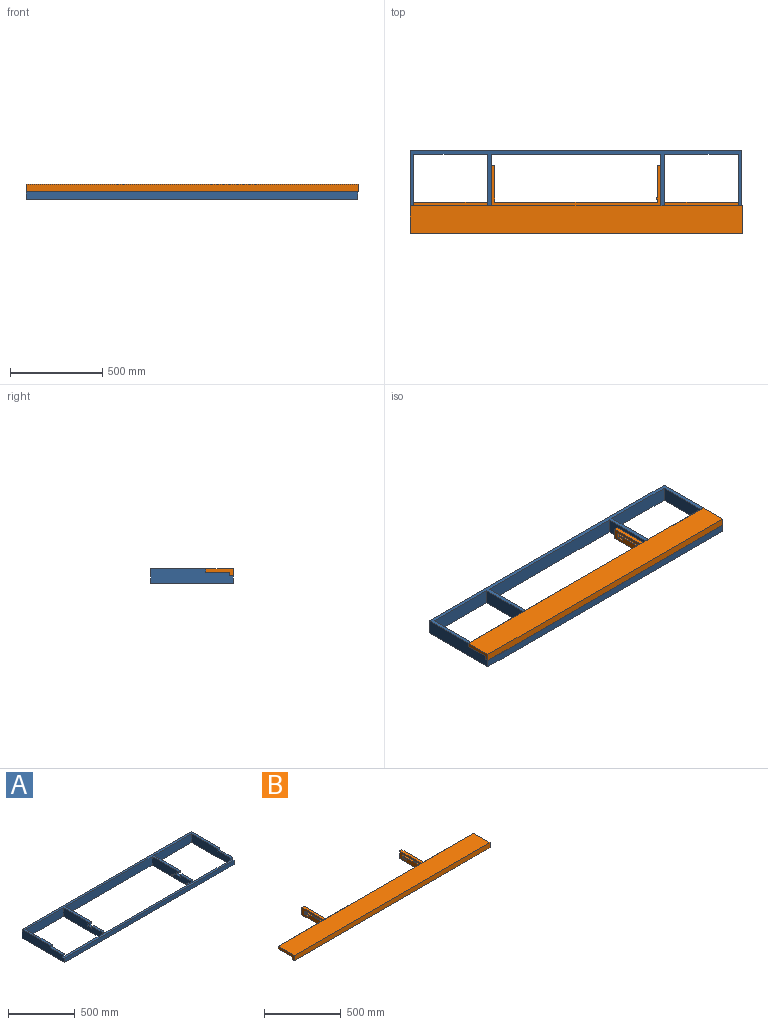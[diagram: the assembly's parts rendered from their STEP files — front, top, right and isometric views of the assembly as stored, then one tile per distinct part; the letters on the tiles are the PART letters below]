
ASSEMBLY  parts=2 mates=1
PART A: 43 faces, bbox 1800x450x80 mm
  f0: plane 410x80mm, normal (-1,0,0), area 29400mm2, adj f2,f6,f7,f12,f18,f24,f28,f39
  f1: plane 410x80mm, normal (1,0,0), area 29400mm2, adj f2,f3,f7,f14,f19,f25,f29,f35
  f2: plane 1800x300mm, normal (0,0,1), area 58400mm2, adj f0,f1,f3,f5,f8,f9,f11,f12
  f3: plane 400x80mm, normal (0,-1,0), area 32000mm2, adj f1,f2,f7,f13
  f4: plane 920x40mm, normal (0,1,0), area 36800mm2, adj f7,f16,f17,f30
  f5: plane 920x80mm, normal (0,-1,0), area 73600mm2, adj f2,f7,f16,f17
  f6: plane 400x40mm, normal (0,1,0), area 16000mm2, adj f0,f7,f15,f30
  f7: plane 1800x450mm, normal (0,0,-1), area 104800mm2, adj f0,f1,f3,f4,f5,f6,f8,f9
  f8: plane 1800x80mm, normal (0,1,0), area 144000mm2, adj f2,f7,f9,f11
  f9: plane 450x80mm, normal (1,0,0), area 32600mm2, adj f2,f7,f8,f10,f21,f22,f26,f30
  f10: plane 1800x40mm, normal (0,-1,0), area 72000mm2, adj f7,f9,f11,f30
  f11: plane 450x80mm, normal (-1,0,0), area 32600mm2, adj f2,f7,f8,f10,f20,f23,f27,f30
  f12: plane 400x80mm, normal (0,-1,0), area 32000mm2, adj f0,f2,f7,f15
  f13: plane 410x80mm, normal (-1,0,0), area 30200mm2, adj f2,f3,f7,f14,f21,f22,f26
  f14: plane 400x40mm, normal (0,1,0), area 16000mm2, adj f1,f7,f13,f30
  f15: plane 410x80mm, normal (1,0,0), area 30200mm2, adj f2,f6,f7,f12,f20,f23,f27
  f16: plane 410x80mm, normal (1,0,0), area 29400mm2, adj f2,f4,f5,f7,f18,f24,f28,f39
  f17: plane 410x80mm, normal (-1,0,0), area 29272.8mm2, adj f2,f4,f5,f7,f19,f25,f29,f31
  f18: plane 20x20mm, normal (0,-1,0), area 400mm2, adj f0,f16,f24,f30
  f19: plane 20x20mm, normal (0,-1,0), area 400mm2, adj f1,f17,f25,f30
  f20: plane 20x20mm, normal (0,-1,0), area 400mm2, adj f11,f15,f23,f30
  f21: plane 20x20mm, normal (0,-1,0), area 400mm2, adj f9,f13,f22,f30
  f22: plane 130x20mm, normal (0,0,1), area 2600mm2, adj f9,f13,f21,f26
  f23: plane 130x20mm, normal (0,0,1), area 2600mm2, adj f11,f15,f20,f27
  f24: plane 110x20mm, normal (0,0,1), area 2200mm2, adj f0,f16,f18,f40
  f25: plane 110x20mm, normal (0,0,1), area 2200mm2, adj f1,f17,f19,f38
  f26: plane 20x20mm, normal (0,-1,0), area 400mm2, adj f2,f9,f13,f22
  f27: plane 20x20mm, normal (0,-1,0), area 400mm2, adj f2,f11,f15,f23
  f28: plane 20x20mm, normal (0,-1,0), area 400mm2, adj f0,f2,f16,f39
  f29: plane 20x20mm, normal (0,-1,0), area 400mm2, adj f1,f2,f17,f35
  f30: plane 1800x20mm, normal (0,0,1), area 36000mm2, adj f4,f6,f9,f10,f11,f14,f18,f19
  f31: cylinder r=4.5mm len=25mm, axis (1,0,0), area 706.9mm2, adj f17,f32
  f32: plane 9x9mm, normal (-1,0,0), area 63.6mm2, adj f31
  f33: cylinder r=4.5mm len=25mm, axis (1,0,0), area 706.9mm2, adj f17,f34
  f34: plane 9x9mm, normal (-1,0,0), area 63.6mm2, adj f33
  f35: plane 20x20mm, normal (0,0,-1), area 400mm2, adj f1,f17,f29,f36
  f36: plane 20x20mm, normal (0,-1,0), area 400mm2, adj f1,f17,f35,f37
  f37: plane 40x20mm, normal (0,0,1), area 800mm2, adj f1,f17,f36,f38
  f38: plane 20x20mm, normal (0,1,0), area 400mm2, adj f1,f17,f25,f37
  f39: plane 20x20mm, normal (0,0,-1), area 400mm2, adj f0,f16,f28,f42
  f40: plane 20x20mm, normal (0,1,0), area 400mm2, adj f0,f16,f24,f41
  f41: plane 40x20mm, normal (0,0,1), area 800mm2, adj f0,f16,f40,f42
  f42: plane 20x20mm, normal (0,-1,0), area 400mm2, adj f0,f16,f39,f41
PART B: 66 faces, bbox 1800x370x80 mm
  f0: plane 880x20mm, normal (0,1,0), area 17600mm2, adj f1,f11,f24,f45
  f1: plane 880x110mm, normal (0,0,-1), area 96800mm2, adj f0,f20,f24,f45
  f2: plane 420x20mm, normal (0,-1,0), area 8400mm2, adj f3,f13,f21,f46
  f3: plane 420x40mm, normal (0,0,-1), area 16800mm2, adj f2,f4,f21,f46
  f4: plane 420x20mm, normal (0,1,0), area 8400mm2, adj f3,f18,f21,f46
  f5: plane 440x20mm, normal (0,1,0), area 8800mm2, adj f6,f11,f16,f25
  f6: plane 440x130mm, normal (0,0,-1), area 48800mm2, adj f5,f7,f14,f16,f19,f25
  f7: plane 420x20mm, normal (0,-1,0), area 8400mm2, adj f6,f8,f19,f25
  f8: plane 420x40mm, normal (0,0,-1), area 16800mm2, adj f7,f9,f19,f25
  f9: plane 420x20mm, normal (0,1,0), area 8400mm2, adj f8,f18,f19,f25
  f10: plane 1800x40mm, normal (0,-1,0), area 72000mm2, adj f11,f15,f16,f17
  f11: plane 1800x20mm, normal (0,0,-1), area 36000mm2, adj f0,f5,f10,f12,f16,f17,f28,f49
  f12: plane 440x20mm, normal (0,1,0), area 8800mm2, adj f11,f13,f17,f46
  f13: plane 440x130mm, normal (0,0,-1), area 48800mm2, adj f2,f12,f14,f17,f21,f46
  f14: plane 1800x20mm, normal (0,1,0), area 36000mm2, adj f6,f13,f15,f16,f17,f18
  f15: plane 1800x150mm, normal (0,0,1), area 270000mm2, adj f10,f14,f16,f17
  f16: plane 150x40mm, normal (1,0,0), area 3400mm2, adj f5,f6,f10,f11,f14,f15
  f17: plane 150x40mm, normal (-1,0,0), area 3400mm2, adj f10,f11,f12,f13,f14,f15
  f18: plane 1760x220mm, normal (0,0,1), area 43200mm2, adj f4,f9,f14,f19,f21,f23,f24,f25
  f19: plane 40x20mm, normal (1,0,0), area 800mm2, adj f6,f7,f8,f9,f18
  f20: plane 880x20mm, normal (0,-1,0), area 17600mm2, adj f1,f22,f24,f45
  f21: plane 40x20mm, normal (-1,0,0), area 800mm2, adj f2,f3,f4,f13,f18
  f22: plane 880x40mm, normal (0,0,-1), area 35200mm2, adj f20,f23,f24,f45
  f23: plane 880x20mm, normal (0,1,0), area 17600mm2, adj f18,f22,f24,f45
  f24: plane 350x60mm, normal (-1,0,0), area 16069.7mm2, adj f0,f1,f18,f20,f22,f23,f26,f27
  f25: plane 350x60mm, normal (1,0,0), area 16069.7mm2, adj f5,f6,f7,f8,f9,f18,f26,f27
  f26: plane 60x20mm, normal (0,1,0), area 1200mm2, adj f18,f24,f25,f27
  f27: plane 326.91x20mm, normal (0,0,-1), area 6538.1mm2, adj f24,f25,f26,f28
  f28: plane 40x23.09mm, normal (0,-0.87,-0.5), area 923.8mm2, adj f11,f24,f25,f27
  f29: plane 20x20mm, normal (0,-1,0), area 400mm2, adj f24,f25,f30,f43
  f30: cylinder r=5mm len=20mm, axis (1,0,0), area 157.1mm2, adj f24,f25,f29,f31
  f31: plane 150x20mm, normal (0,0,-1), area 3000mm2, adj f24,f25,f30,f32
  f32: cylinder r=5mm len=20mm, axis (1,0,0), area 314.2mm2, adj f24,f25,f31,f33
  f33: plane 145x20mm, normal (0,0,1), area 2900mm2, adj f24,f25,f32,f34
  f34: plane 20x10mm, normal (0,1,0), area 200mm2, adj f24,f25,f33,f35
  f35: plane 25x20mm, normal (0,0,-1), area 500mm2, adj f24,f25,f34,f36
  f36: cylinder r=5mm len=20mm, axis (1,0,0), area 314.2mm2, adj f24,f25,f35,f37
  f37: plane 30x20mm, normal (0,0,1), area 600mm2, adj f24,f25,f36,f43
  f38: cylinder r=375mm len=121.62mm, axis (1,0,0), area 2477.2mm2, adj f24,f25,f39,f44
  f39: plane 30x20mm, normal (0,0,1), area 600mm2, adj f24,f25,f38,f40
  f40: cylinder r=5mm len=20mm, axis (1,0,0), area 314.2mm2, adj f24,f25,f39,f41
  f41: plane 30x20mm, normal (0,0,-1), area 600mm2, adj f24,f25,f40,f42
  f42: cylinder r=365mm len=118.38mm, axis (1,0,0), area 2411.2mm2, adj f24,f25,f41,f44
  f43: cylinder r=5mm len=20mm, axis (1,0,0), area 157.1mm2, adj f24,f25,f29,f37
  f44: cylinder r=5mm len=20mm, axis (1,0,0), area 314.2mm2, adj f24,f25,f38,f42
  f45: plane 350x60mm, normal (1,0,0), area 16069.7mm2, adj f0,f1,f18,f20,f22,f23,f47,f48
  f46: plane 350x60mm, normal (-1,0,0), area 16069.7mm2, adj f2,f3,f4,f12,f13,f18,f47,f48
  f47: plane 60x20mm, normal (0,1,0), area 1200mm2, adj f18,f45,f46,f48
  f48: plane 326.91x20mm, normal (0,0,-1), area 6538.1mm2, adj f45,f46,f47,f49
  f49: plane 40x23.09mm, normal (0,-0.87,-0.5), area 923.8mm2, adj f11,f45,f46,f48
  f50: plane 20x20mm, normal (0,-1,0), area 400mm2, adj f45,f46,f51,f64
  f51: cylinder r=5mm len=20mm, axis (-1,0,0), area 157.1mm2, adj f45,f46,f50,f52
  f52: plane 150x20mm, normal (0,0,-1), area 3000mm2, adj f45,f46,f51,f53
  f53: cylinder r=5mm len=20mm, axis (-1,0,0), area 314.2mm2, adj f45,f46,f52,f54
  f54: plane 145x20mm, normal (0,0,1), area 2900mm2, adj f45,f46,f53,f55
  f55: plane 20x10mm, normal (0,1,0), area 200mm2, adj f45,f46,f54,f56
  f56: plane 25x20mm, normal (0,0,-1), area 500mm2, adj f45,f46,f55,f57
  f57: cylinder r=5mm len=20mm, axis (-1,0,0), area 314.2mm2, adj f45,f46,f56,f58
  f58: plane 30x20mm, normal (0,0,1), area 600mm2, adj f45,f46,f57,f64
  f59: cylinder r=375mm len=121.62mm, axis (-1,0,0), area 2477.2mm2, adj f45,f46,f60,f65
  f60: plane 30x20mm, normal (0,0,1), area 600mm2, adj f45,f46,f59,f61
  f61: cylinder r=5mm len=20mm, axis (-1,0,0), area 314.2mm2, adj f45,f46,f60,f62
  f62: plane 30x20mm, normal (0,0,-1), area 600mm2, adj f45,f46,f61,f63
  f63: cylinder r=365mm len=118.38mm, axis (-1,0,0), area 2411.2mm2, adj f45,f46,f62,f65
  f64: cylinder r=5mm len=20mm, axis (-1,0,0), area 157.1mm2, adj f45,f46,f50,f58
  f65: cylinder r=5mm len=20mm, axis (-1,0,0), area 314.2mm2, adj f45,f46,f59,f63
PLACE A at identity fixed
PLACE B rot(axis=(-1,0,0),0.4deg) t=(0,0.46,-2.05)mm
MATE planar A.f9 <-> B.f16  axis (1,0,0) through (900,-208.56,-42.88)mm
